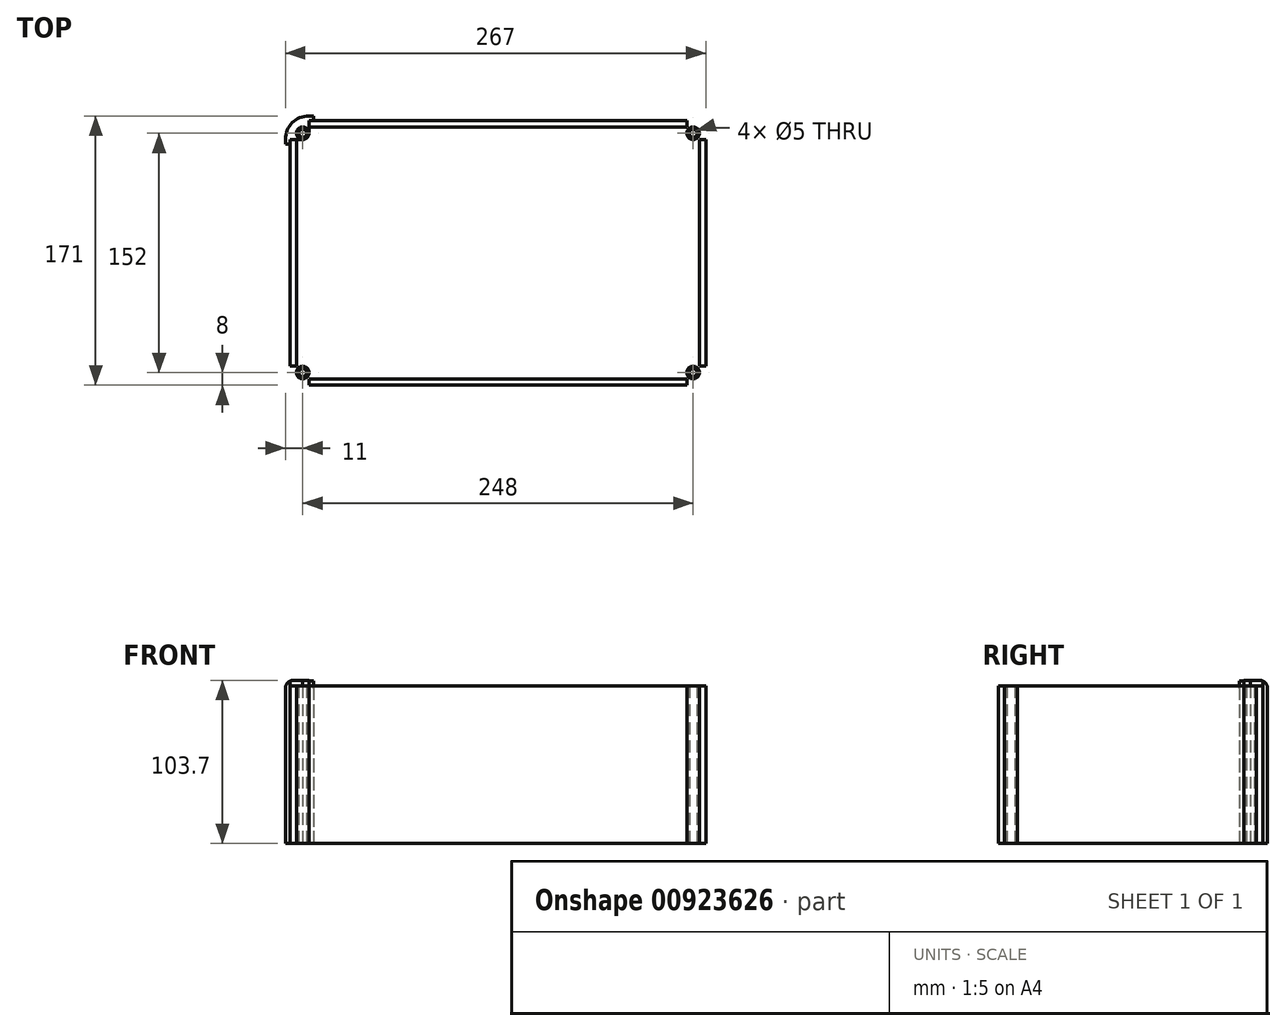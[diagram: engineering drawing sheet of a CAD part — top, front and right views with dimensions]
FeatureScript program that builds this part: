
annotation { "Feature Type Name" : "Feature", "Feature Type Description" : "" }
export const myFeature = defineFeature(function(context is Context, id is Id, definition is map)
    precondition{}
    {
        {
            var Q0;
            Q0=qCreatedBy(makeId("Top.planeOp"),FACE);
            var sketch = newSketch(context, id + "F0", { "sketchPlane" : qUnion([Q0])});
            skLineSegment(sketch, "E0.bottom", {"start": v(128, 80) * mm, "end": v(-128, 80) * mm, "construction": true});
            skLineSegment(sketch, "E0.top", {"start": v(128, -80) * mm, "end": v(-128, -80) * mm, "construction": true});
            skLineSegment(sketch, "E0.left", {"start": v(128, 80) * mm, "end": v(128, -80) * mm, "construction": true});
            skLineSegment(sketch, "E0.right", {"start": v(-128, 80) * mm, "end": v(-128, -80) * mm, "construction": true});
            skPoint(sketch, "E0.middle", {"position": v(0, 0) * mm});
            skLineSegment(sketch, "E1.0", {"start": v(124, 76) * mm, "end": v(124, -76) * mm, "construction": true});
            skLineSegment(sketch, "E1.1", {"start": v(124, 76) * mm, "end": v(-124, 76) * mm, "construction": true});
            skLineSegment(sketch, "E1.2", {"start": v(-124, 76) * mm, "end": v(-124, -76) * mm, "construction": true});
            skLineSegment(sketch, "E1.3", {"start": v(124, -76) * mm, "end": v(-124, -76) * mm, "construction": true});
            skCircle(sketch, "E2", {"center": v(-124, 76) * mm, "radius": 4 * mm});
            skCircle(sketch, "E3", {"center": v(-124, -76) * mm, "radius": 4 * mm});
            skCircle(sketch, "E4", {"center": v(124, -76) * mm, "radius": 4 * mm});
            skCircle(sketch, "E5", {"center": v(124, 76) * mm, "radius": 4 * mm});
            skCircle(sketch, "E6", {"center": v(124, 76) * mm, "radius": 2.5 * mm});
            skCircle(sketch, "E7", {"center": v(124, -76) * mm, "radius": 2.5 * mm});
            skCircle(sketch, "E8", {"center": v(-124, -76) * mm, "radius": 2.5 * mm});
            skCircle(sketch, "E9", {"center": v(-124, 76) * mm, "radius": 2.5 * mm});
            skLineSegment(sketch, "E10", {"start": v(120, -80) * mm, "end": v(120, 80) * mm, "construction": true});
            skLineSegment(sketch, "E11", {"start": v(-128, -72) * mm, "end": v(128, -72) * mm, "construction": true});
            skLineSegment(sketch, "E12", {"start": v(-120, -80) * mm, "end": v(-120, 80) * mm, "construction": true});
            skLineSegment(sketch, "E13", {"start": v(-128, 72) * mm, "end": v(128, 72) * mm, "construction": true});
            skLineSegment(sketch, "E14.bottom", {"start": v(128, 72) * mm, "end": v(132, 72) * mm});
            skLineSegment(sketch, "E14.top", {"start": v(128, -72) * mm, "end": v(132, -72) * mm});
            skLineSegment(sketch, "E14.left", {"start": v(128, 72) * mm, "end": v(128, -72) * mm});
            skLineSegment(sketch, "E14.right", {"start": v(132, 72) * mm, "end": v(132, -72) * mm});
            skLineSegment(sketch, "E15.bottom", {"start": v(120, -80) * mm, "end": v(-120, -80) * mm});
            skLineSegment(sketch, "E15.top", {"start": v(120, -84) * mm, "end": v(-120, -84) * mm});
            skLineSegment(sketch, "E15.left", {"start": v(120, -80) * mm, "end": v(120, -84) * mm});
            skLineSegment(sketch, "E15.right", {"start": v(-120, -80) * mm, "end": v(-120, -84) * mm});
            skLineSegment(sketch, "E16.bottom", {"start": v(-128, -72) * mm, "end": v(-132, -72) * mm});
            skLineSegment(sketch, "E16.top", {"start": v(-128, 72) * mm, "end": v(-132, 72) * mm});
            skLineSegment(sketch, "E16.left", {"start": v(-128, -72) * mm, "end": v(-128, 72) * mm});
            skLineSegment(sketch, "E16.right", {"start": v(-132, -72) * mm, "end": v(-132, 72) * mm});
            skLineSegment(sketch, "E17.bottom", {"start": v(-120, 80) * mm, "end": v(120, 80) * mm});
            skLineSegment(sketch, "E17.top", {"start": v(-120, 84) * mm, "end": v(120, 84) * mm});
            skLineSegment(sketch, "E17.left", {"start": v(-120, 80) * mm, "end": v(-120, 84) * mm});
            skLineSegment(sketch, "E17.right", {"start": v(120, 80) * mm, "end": v(120, 84) * mm});
            skLineSegment(sketch, "E18", {"start": v(128, -72) * mm, "end": v(124, -72) * mm, "construction": true});
            skArc(sketch, "E19", {"start": v(-120, 84) * mm, "mid": v(-128.49, 80.49) * mm, "end": v(-132, 72) * mm, "construction": true});
            skArc(sketch, "E20.0", {"start": v(-120, 87) * mm, "mid": v(-130.6, 82.6) * mm, "end": v(-135, 72) * mm});
            skLineSegment(sketch, "E21", {"start": v(-135, 72) * mm, "end": v(-135, 69) * mm});
            skLineSegment(sketch, "E22", {"start": v(-135, 69) * mm, "end": v(-132, 69) * mm});
            skLineSegment(sketch, "E23", {"start": v(-120, 87) * mm, "end": v(-117, 87) * mm});
            skLineSegment(sketch, "E24", {"start": v(-117, 87) * mm, "end": v(-117, 84) * mm});
            skLineSegment(sketch, "E25", {"start": v(-132, 69) * mm, "end": v(-132, 72) * mm});
            skLineSegment(sketch, "E26", {"start": v(-132, 72) * mm, "end": v(-120, 72) * mm});
            skLineSegment(sketch, "E27", {"start": v(-120, 72) * mm, "end": v(-120, 84) * mm});
            skSolve(sketch);
        }
        {
            var Q0;
            Q0=makeQuery(id+"F0.imprint","IMPRINT",FACE,{"disambiguationData":[TD([[makeQuery(id+"F0.imprint","IMPRINT",EDGE,{"derivedFrom":sQuery(id+"F0.wireOp",EDGE,"E2")}),1.0]])]});
            var Q1;
            Q1=makeQuery(id+"F0.imprint","IMPRINT",FACE,{"disambiguationData":[TD([[makeQuery(id+"F0.imprint","IMPRINT",EDGE,{"derivedFrom":sQuery(id+"F0.wireOp",EDGE,"E3")}),1.0]])]});
            var Q2;
            Q2=makeQuery(id+"F0.imprint","IMPRINT",FACE,{"disambiguationData":[TD([[makeQuery(id+"F0.imprint","IMPRINT",EDGE,{"derivedFrom":sQuery(id+"F0.wireOp",EDGE,"E4")}),1.0]])]});
            var Q3;
            Q3=makeQuery(id+"F0.imprint","IMPRINT",FACE,{"disambiguationData":[TD([[makeQuery(id+"F0.imprint","IMPRINT",EDGE,{"derivedFrom":sQuery(id+"F0.wireOp",EDGE,"E5")}),1.0]])]});
            var Q4;
            Q4=makeQuery(id+"F0.imprint","IMPRINT",FACE,{"disambiguationData":[TD([[makeQuery(id+"F0.imprint","IMPRINT",EDGE,{"derivedFrom":sQuery(id+"F0.wireOp",EDGE,"E17.bottom")}),1.0]])]});
            var Q5;
            Q5=makeQuery(id+"F0.imprint","IMPRINT",FACE,{"disambiguationData":[TD([[makeQuery(id+"F0.imprint","IMPRINT",EDGE,{"derivedFrom":sQuery(id+"F0.wireOp",EDGE,"E16.bottom")}),-1.0]])]});
            var Q6;
            Q6=makeQuery(id+"F0.imprint","IMPRINT",FACE,{"disambiguationData":[TD([[makeQuery(id+"F0.imprint","IMPRINT",EDGE,{"derivedFrom":sQuery(id+"F0.wireOp",EDGE,"E15.bottom")}),1.0]])]});
            var Q7;
            Q7=makeQuery(id+"F0.imprint","IMPRINT",FACE,{"disambiguationData":[TD([[makeQuery(id+"F0.imprint","IMPRINT",EDGE,{"derivedFrom":sQuery(id+"F0.wireOp",EDGE,"E14.bottom")}),-1.0]])]});
            extrude(context, id + "F1", {"entities" : qUnion([Q0, Q1, Q2, Q3, Q4, Q5, Q6, Q7]), "depth" : 100 * mm, "offsetDistance" : 25 * mm});
        }
        {
            var Q0;
            Q0=makeQuery(id+"F0.imprint","IMPRINT",FACE,{"disambiguationData":[TD([[makeQuery(id+"F0.imprint","IMPRINT",EDGE,{"derivedFrom":sQuery(id+"F0.wireOp",EDGE,"E20.0")}),1.0]])]});
            extrude(context, id + "F2", {"entities" : qUnion([Q0]), "depth" : 103.7 * mm, "offsetDistance" : 25 * mm});
        }
        {
            var Q0;
            Q0=makeQuery(id+"F2.opExtrude","CAP_EDGE",EDGE,{"disambiguationData":[OSD([sQuery(id+"F0.wireOp",EDGE,"E20.0")])],"isStart":false});
            fillet(context, id + "F3", {"entities" : qUnion([Q0]), "radius" : 5 * mm, "tangentPropagation" : true, "allowEdgeOverflow" : false});
        }
    });
